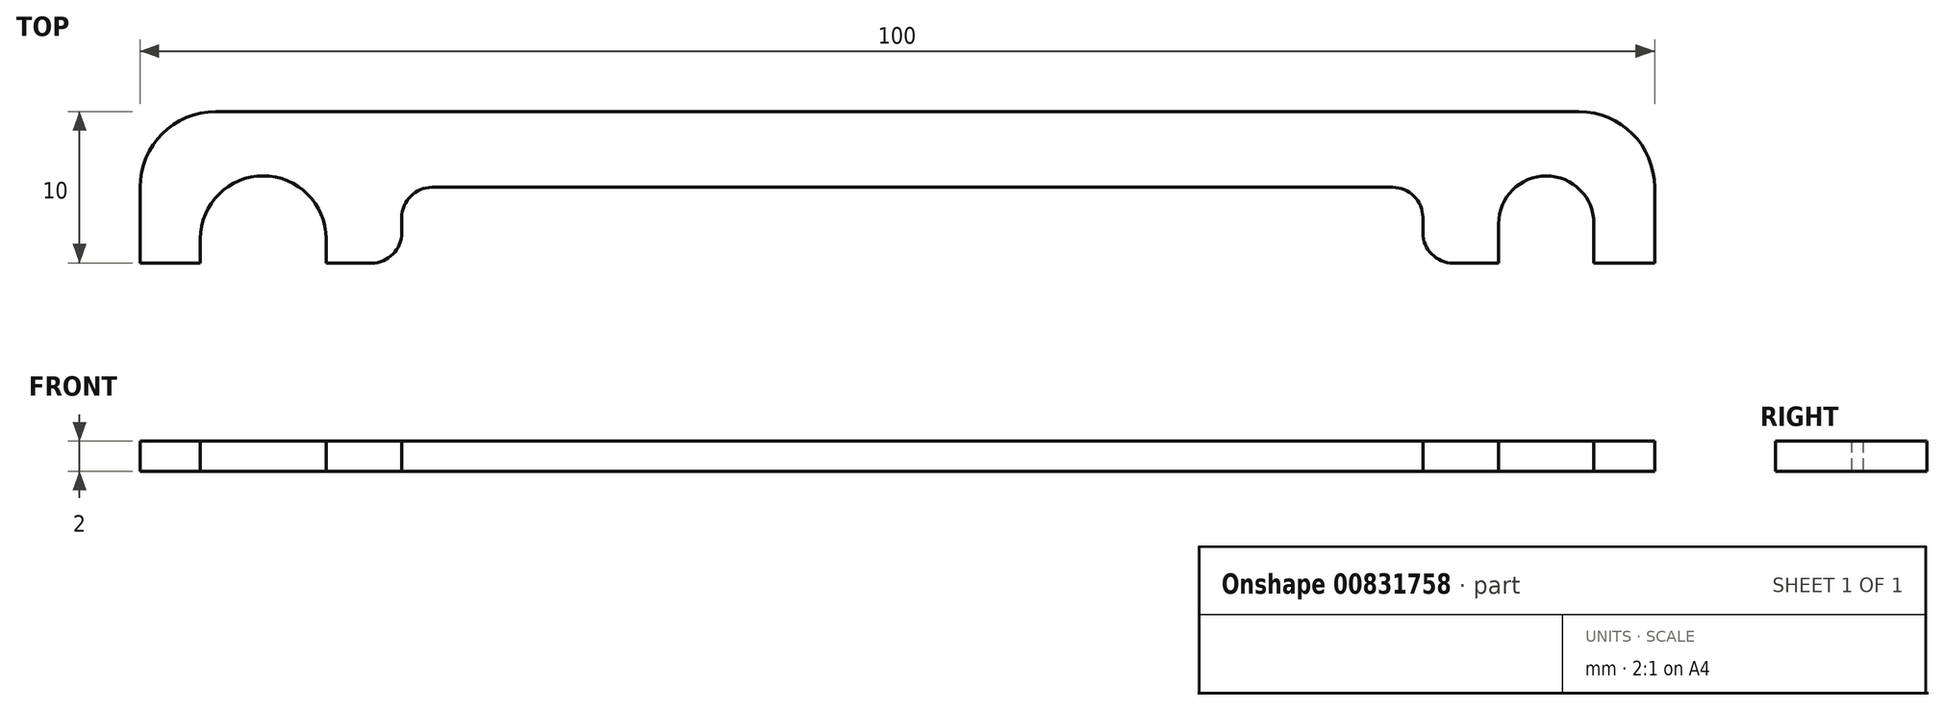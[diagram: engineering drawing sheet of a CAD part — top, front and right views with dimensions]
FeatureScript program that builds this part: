
annotation { "Feature Type Name" : "Feature", "Feature Type Description" : "" }
export const myFeature = defineFeature(function(context is Context, id is Id, definition is map)
    precondition{}
    {
        {
            var Q0;
            Q0=qCreatedBy(makeId("Top.planeOp"),FACE);
            var sketch = newSketch(context, id + "F0", { "sketchPlane" : qUnion([Q0])});
            skLineSegment(sketch, "E0.bottom", {"start": v(45, 5) * mm, "end": v(-45, 5) * mm});
            skLineSegment(sketch, "E0.top", {"start": v(50, -5) * mm, "end": v(46, -5) * mm});
            skLineSegment(sketch, "E0.left", {"start": v(50, 0) * mm, "end": v(50, -5) * mm});
            skLineSegment(sketch, "E0.right", {"start": v(-50, 0) * mm, "end": v(-50, -5) * mm});
            skPoint(sketch, "E0.middle", {"position": v(0, 0) * mm});
            skPoint(sketch, "E1.visualSharp", {"position": v(-50, 5) * mm});
            skArc(sketch, "E1.filletArc", {"start": v(-45, 5) * mm, "mid": v(-48.54, 3.54) * mm, "end": v(-50, 0) * mm});
            skPoint(sketch, "E2.visualSharp", {"position": v(50, 5) * mm});
            skArc(sketch, "E2.filletArc", {"start": v(50, 0) * mm, "mid": v(48.54, 3.54) * mm, "end": v(45, 5) * mm});
            skArc(sketch, "E3", {"start": v(-37.72, -3.4) * mm, "mid": v(-41.87, 0.75) * mm, "end": v(-46.02, -3.4) * mm});
            skArc(sketch, "E4", {"start": v(46, -2.4) * mm, "mid": v(42.85, 0.75) * mm, "end": v(39.7, -2.4) * mm});
            skLineSegment(sketch, "E5", {"start": v(-50, 0.75) * mm, "end": v(-49.94, 0.75) * mm});
            skLineSegment(sketch, "E6", {"start": v(-46.02, -5) * mm, "end": v(-46.02, -3.4) * mm});
            skLineSegment(sketch, "E7", {"start": v(-37.72, -5) * mm, "end": v(-37.72, -3.4) * mm});
            skLineSegment(sketch, "E8", {"start": v(39.7, -5) * mm, "end": v(39.7, -2.4) * mm});
            skLineSegment(sketch, "E9", {"start": v(46, -5) * mm, "end": v(46, -2.4) * mm});
            skLineSegment(sketch, "E10.trimOffspring", {"start": v(-46.02, -5) * mm, "end": v(-50, -5) * mm});
            skLineSegment(sketch, "E11.trimOffspring", {"start": v(39.7, -5) * mm, "end": v(36.7, -5) * mm});
            skLineSegment(sketch, "E12.trimOffspring", {"start": v(49.94, 0.75) * mm, "end": v(50, 0.75) * mm});
            skLineSegment(sketch, "E13", {"start": v(-32.72, -3) * mm, "end": v(-32.72, -2) * mm});
            skLineSegment(sketch, "E14", {"start": v(-30.72, 0) * mm, "end": v(32.7, 0) * mm});
            skLineSegment(sketch, "E15", {"start": v(34.7, -2) * mm, "end": v(34.7, -3) * mm});
            skLineSegment(sketch, "E16.trimOffspring", {"start": v(-34.72, -5) * mm, "end": v(-37.72, -5) * mm});
            skPoint(sketch, "E17.visualSharp", {"position": v(-32.72, -5) * mm});
            skArc(sketch, "E17.filletArc", {"start": v(-34.72, -5) * mm, "mid": v(-33.3, -4.41) * mm, "end": v(-32.72, -3) * mm});
            skPoint(sketch, "E18.visualSharp", {"position": v(34.7, -5) * mm});
            skArc(sketch, "E18.filletArc", {"start": v(34.7, -3) * mm, "mid": v(35.29, -4.41) * mm, "end": v(36.7, -5) * mm});
            skPoint(sketch, "E19.visualSharp", {"position": v(-32.72, 0) * mm});
            skArc(sketch, "E19.filletArc", {"start": v(-30.72, 0) * mm, "mid": v(-32.13, -0.59) * mm, "end": v(-32.72, -2) * mm});
            skPoint(sketch, "E20.visualSharp", {"position": v(34.7, 0) * mm});
            skArc(sketch, "E20.filletArc", {"start": v(34.7, -2) * mm, "mid": v(34.11, -0.59) * mm, "end": v(32.7, 0) * mm});
            skSolve(sketch);
        }
        {
            var Q0;
            {var subQ1=sQuery(id+"F0.wireOp",EDGE,"E0.bottom");Q0=makeQuery(id+"F0.imprint","IMPRINT",FACE,{"disambiguationData":[TD([[makeQuery(id+"F0.imprint","IMPRINT",EDGE,{"derivedFrom":subQ1}),1.0]])]});}
            extrude(context, id + "F1", {"entities" : qUnion([Q0]), "depth" : 2 * mm, "offsetDistance" : 25.4 * mm});
        }
    });
